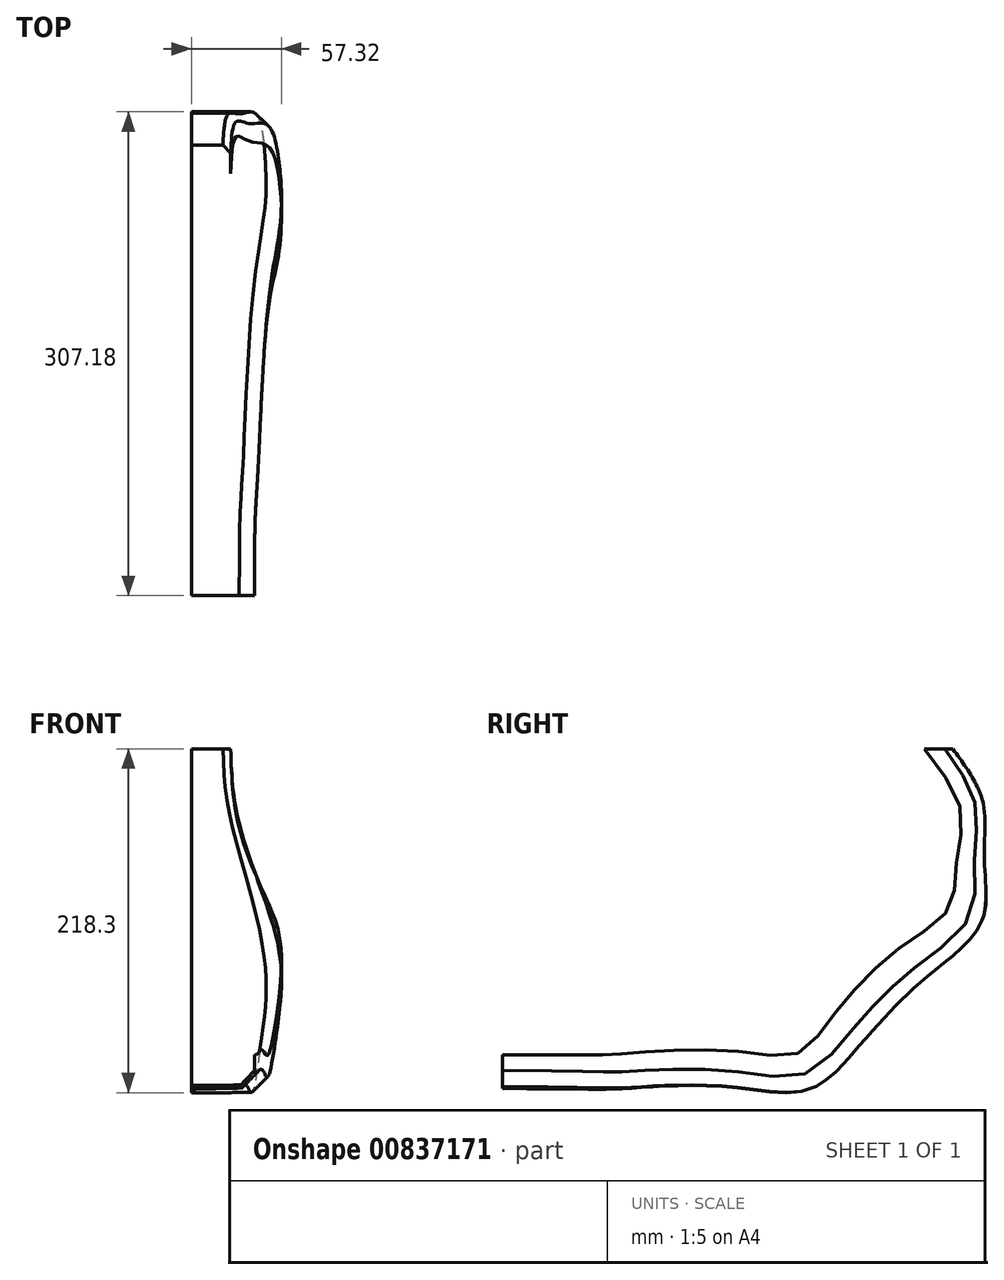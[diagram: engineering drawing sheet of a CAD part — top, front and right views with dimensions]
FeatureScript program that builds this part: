
annotation { "Feature Type Name" : "Feature", "Feature Type Description" : "" }
export const myFeature = defineFeature(function(context is Context, id is Id, definition is map)
    precondition{}
    {
        {
            var Q0;
            Q0=qCreatedBy(makeId("Right.planeOp"),FACE);
            var sketch = newSketch(context, id + "F0", { "sketchPlane" : qUnion([Q0])});
            skLineSegment(sketch, "E0", {"start": v(0, 0) * mm, "end": v(17.32, -30) * mm});
            skLineSegment(sketch, "E1", {"start": v(20, -40) * mm, "end": v(20, -101.36) * mm});
            skLineSegment(sketch, "E2", {"start": v(14.14, -115.5) * mm, "end": v(-80.2, -209.85) * mm});
            skLineSegment(sketch, "E3", {"start": v(-94.35, -215.7) * mm, "end": v(-286.07, -215.7) * mm});
            skPoint(sketch, "E4.visualSharp", {"position": v(20, -34.64) * mm});
            skArc(sketch, "E4.filletArc", {"start": v(20, -40) * mm, "mid": v(19.32, -34.82) * mm, "end": v(17.32, -30) * mm});
            skPoint(sketch, "E5.visualSharp", {"position": v(20, -109.64) * mm});
            skArc(sketch, "E5.filletArc", {"start": v(14.14, -115.5) * mm, "mid": v(18.48, -109.01) * mm, "end": v(20, -101.36) * mm});
            skPoint(sketch, "E6.visualSharp", {"position": v(-86.07, -215.7) * mm});
            skArc(sketch, "E6.filletArc", {"start": v(-94.35, -215.7) * mm, "mid": v(-86.7, -214.18) * mm, "end": v(-80.2, -209.85) * mm});
            skLineSegment(sketch, "E7", {"start": v(20, -109.64) * mm, "end": v(0, -101.36) * mm, "construction": true});
            skLineSegment(sketch, "E8", {"start": v(24.3, -53.44) * mm, "end": v(19.32, -34.82) * mm, "construction": true});
            skLineSegment(sketch, "E9", {"start": v(0, -40) * mm, "end": v(20, -34.64) * mm, "construction": true});
            skLineSegment(sketch, "E10", {"start": v(18.48, -109.01) * mm, "end": v(25.12, -92.98) * mm, "construction": true});
            skLineSegment(sketch, "E11", {"start": v(-94.35, -195.7) * mm, "end": v(-86.07, -215.7) * mm, "construction": true});
            skLineSegment(sketch, "E12", {"start": v(-86.7, -214.18) * mm, "end": v(-58.84, -202.65) * mm, "construction": true});
            skSolve(sketch);
        }
        {
            var Q0;
            Q0=sQuery(id+"F0.wireOp",VERTEX,"E8.end");
            var Q1;
            Q1=sQuery(id+"F0.wireOp",EDGE,"E4.filletArc");
            cPlane(context, id + "F1", {"entities" : qUnion([Q0, Q1]), "cplaneType" : CPlaneType.CURVE_POINT, "offset" : 25 * mm, "width" : 150 * mm, "height" : 150 * mm});
        }
        {
            var Q0;
            Q0=sQuery(id+"F0.wireOp",EDGE,"E5.filletArc");
            var Q1;
            Q1=sQuery(id+"F0.wireOp",VERTEX,"E10.start");
            cPlane(context, id + "F2", {"entities" : qUnion([Q0, Q1]), "cplaneType" : CPlaneType.CURVE_POINT, "offset" : 25 * mm, "width" : 150 * mm, "height" : 150 * mm});
        }
        {
            var Q0;
            Q0=sQuery(id+"F0.wireOp",EDGE,"E6.filletArc");
            var Q1;
            Q1=sQuery(id+"F0.wireOp",VERTEX,"E12.start");
            cPlane(context, id + "F3", {"entities" : qUnion([Q0, Q1]), "cplaneType" : CPlaneType.CURVE_POINT, "offset" : 25 * mm, "width" : 150 * mm, "height" : 150 * mm});
        }
        {
            var Q0;
            Q0=sQuery(id+"F0.wireOp",VERTEX,"E3.end");
            var Q1;
            Q1=qCreatedBy(makeId("Front.planeOp"),FACE);
            cPlane(context, id + "F4", {"entities" : qUnion([Q0, Q1]), "cplaneType" : CPlaneType.PLANE_POINT, "offset" : 25 * mm, "width" : 150 * mm, "height" : 150 * mm});
        }
        {
            var Q0;
            Q0=qCreatedBy(makeId("Top.planeOp"),FACE);
            var sketch = newSketch(context, id + "F5", { "sketchPlane" : qUnion([Q0])});
            skLineSegment(sketch, "E13", {"start": v(0, 0) * mm, "end": v(20, 0) * mm});
            skLineSegment(sketch, "E14", {"start": v(25, -5) * mm, "end": v(25, -18) * mm});
            skLineSegment(sketch, "E15", {"start": v(20, 0) * mm, "end": v(25, -5) * mm});
            skSolve(sketch);
        }
        {
            var Q0;
            Q0=qCreatedBy(id+"F1.planeOp",FACE);
            var sketch = newSketch(context, id + "F6", { "sketchPlane" : qUnion([Q0])});
            skLineSegment(sketch, "E16", {"start": v(0, 9.65) * mm, "end": v(23, 9.65) * mm});
            skLineSegment(sketch, "E17", {"start": v(28, 4.65) * mm, "end": v(28, -5.35) * mm});
            skLineSegment(sketch, "E18", {"start": v(23, 9.65) * mm, "end": v(28, 4.65) * mm});
            skSolve(sketch);
        }
        {
            var Q0;
            Q0=qCreatedBy(id+"F2.planeOp",FACE);
            var sketch = newSketch(context, id + "F7", { "sketchPlane" : qUnion([Q0])});
            skLineSegment(sketch, "E19", {"start": v(0, 58.79) * mm, "end": v(42, 58.79) * mm});
            skLineSegment(sketch, "E20", {"start": v(50, 36.79) * mm, "end": v(50, 50.79) * mm});
            skLineSegment(sketch, "E21", {"start": v(42, 58.79) * mm, "end": v(50, 50.79) * mm});
            skPoint(sketch, "E22.orphan", {"position": v(50, 58.79) * mm});
            skSolve(sketch);
        }
        {
            var Q0;
            Q0=qCreatedBy(id+"F3.planeOp",FACE);
            var sketch = newSketch(context, id + "F8", { "sketchPlane" : qUnion([Q0])});
            skLineSegment(sketch, "E23", {"start": v(0, -164.7) * mm, "end": v(-40, -164.7) * mm});
            skLineSegment(sketch, "E24", {"start": v(-50, -154.7) * mm, "end": v(-50, -140.7) * mm});
            skLineSegment(sketch, "E25", {"start": v(-40, -164.7) * mm, "end": v(-50, -154.7) * mm});
            skSolve(sketch);
        }
        {
            var Q0;
            Q0=qCreatedBy(id+"F4.planeOp",FACE);
            var sketch = newSketch(context, id + "F9", { "sketchPlane" : qUnion([Q0])});
            skLineSegment(sketch, "E26", {"start": v(0, -215.7) * mm, "end": v(30.39, -214.55) * mm});
            skLineSegment(sketch, "E27", {"start": v(40, -204.18) * mm, "end": v(40, -194.17) * mm});
            skLineSegment(sketch, "E28", {"start": v(30.39, -214.55) * mm, "end": v(40, -204.18) * mm});
            skPoint(sketch, "E29.orphan", {"position": v(40, -214.18) * mm});
            skSolve(sketch);
        }
        {
            var Q0;
            Q0 = qConstructionFilter(qBodyType(qCreatedBy(id + "F0" ,EDGE), BodyType.WIRE), ConstructionObject.NO);
            var Q1;
            Q1 = qSketchRegion(id + "F5", true);
            var Q2;
            Q2 = qSketchRegion(id + "F6", true);
            var Q3;
            Q3 = qSketchRegion(id + "F8", true);
            var Q4;
            Q4 = qSketchRegion(id + "F9", true);
            var Q5;
            Q5 = qConstructionFilter(qBodyType(qCreatedBy(id + "F5" ,EDGE), BodyType.WIRE), ConstructionObject.NO);
            var Q6;
            Q6 = qConstructionFilter(qBodyType(qCreatedBy(id + "F6" ,EDGE), BodyType.WIRE), ConstructionObject.NO);
            var Q7;
            Q7 = qConstructionFilter(qBodyType(qCreatedBy(id + "F7" ,EDGE), BodyType.WIRE), ConstructionObject.NO);
            var Q8;
            Q8 = qConstructionFilter(qBodyType(qCreatedBy(id + "F8" ,EDGE), BodyType.WIRE), ConstructionObject.NO);
            var Q9;
            Q9 = qConstructionFilter(qBodyType(qCreatedBy(id + "F9" ,EDGE), BodyType.WIRE), ConstructionObject.NO);
            loft(context, id + "F10", {"bodyType" : ToolBodyType.SURFACE, "addSections" : true, "spine" : qUnion([Q0]), "sectionCount" : 5, "endCondition" : LoftEndDerivativeType.NORMAL_TO_PROFILE, "endMagnitude" : 2, "sheetProfilesArray" : [{ "sheetProfileEntities" : qUnion([Q1]) }, { "sheetProfileEntities" : qUnion([Q2]) }, { "sheetProfileEntities" : qUnion([Q3]) }, { "sheetProfileEntities" : qUnion([Q4]) }], "wireProfilesArray" : [{ "wireProfileEntities" : qUnion([Q5]) }, { "wireProfileEntities" : qUnion([Q6]) }, { "wireProfileEntities" : qUnion([Q7]) }, { "wireProfileEntities" : qUnion([Q8]) }, { "wireProfileEntities" : qUnion([Q9]) }]});
        }
    });
